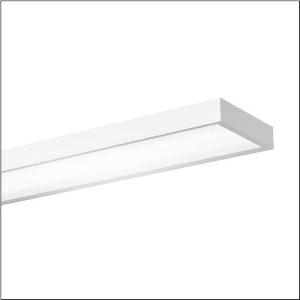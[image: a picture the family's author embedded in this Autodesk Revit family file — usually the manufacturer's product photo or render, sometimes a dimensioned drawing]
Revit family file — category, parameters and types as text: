
# Revit family: sport_31_51hs12dd4gca
name_source: partatom
category: Lighting Fixtures
units: mm (PartAtom-declared; Revit-internal decimal feet)

## family parameters
Cut with Voids When Loaded = No
Host = Face
Light Source = No
Part Type = Normal
Room Calculation Point = No
Round Connector Dimension = Use Diameter
Shared = No

## types (1)
- --- (1 x LED, 15290 lm, 113 W, 4000K)
    Apparent Load = 113 VA
    CIE Flux Codes = 65 89 97 100 100
    Color Rendering = 80
    Color Temperature = 4000K
    Default Elevation = 1800 mm
    Description = Sport 31, LED high bay luminaire, primary light control with reflector, of sheet steel, primary anti-glare with prismatic structure, of PC, primary optical cover: cover panel, of PC, light emission: direct distribution, primary light characteristic: symmetric, installation type: suspended mounting, recessed, surface-mounted, LED, rated luminous flux: 16.000lm, luminous efficacy: 137lm/W, light colour: 840, colour temperature: 4000K, control gear: ECG DALI, with terminal, 5-pole, max. 2.5mm², mains connection: 220..240V, AC/DC, 50/60Hz, rated input power: 117W, housing, of sheet steel, traffic white (RAL 9016), length: 1.540mm, width: 415mm, height: 95mm, protection rating (complete): IP20, protection rating (lamp compartment, on room side): IP50, insulation class (complete): insulation class I (protective earthing), certification: CE, ENEC, UKCA, ball protection: ball impact resistant with ceiling mounting or chain suspension, impact resistance: IK08, permissible operating ambient temperature: -20..+35°C, standard: DIN 18032-3, EN 60598-2-22, packaging unit: 1 piece
    Height = 100 mm  [stored 0.328084 ft]
    Lamp = 1 x LED
    Lamp Light Flux = 15290 lm
    Lamp Power = 113 W
    Lamp count = 1
    Length = 1500 mm
    Luminous efficacy = 135 lm/W
    Manufacturer = Siteco
    ModVariant = No
    Model = 51HS12DD4GCA
    Mounting Place = Ceiling
    Mounting Type = Pendant
    Number of Poles = 1
    OnlyDefault = Yes
    Power Factor = 1
    Product Name = Sport 31
    Product group = LED high bay luminaire
    ProductGroupID = 903
    Protection Class = Protection class I
    Protection Degree = IP 20
    RLX_Detail_Level = 1
    RLX_Emergency_Light_Flux = 0 lm
    RLX_Emergency_Type = 0
    RLX_Emergency_Type_DB = No
    RlxData = <blob elided: 24141 chars, md5=40534fce>
    Socket = socket
    Standby Power = 0 W
    System Light Flux = 15290 lm
    System Power = 113 W
    Type Comments = factory setting: luminous flux: 100 % | dim-lin: 254 | 558 mA
    Type Image = l_1006829.jpg
    URL = http://relux.com
    VarID = @adj_170139
    Voltage = 0 V
    Weight = 0.00 kg
    Width = 415 mm

note: [stored X ft] marks values corroborated as IEEE doubles in the binary element streams (Revit-internal decimal feet)

## geometry (parser evidence)
native form markers: Blend x4, Sweep x10
no freeform markers — native parametric forms only
